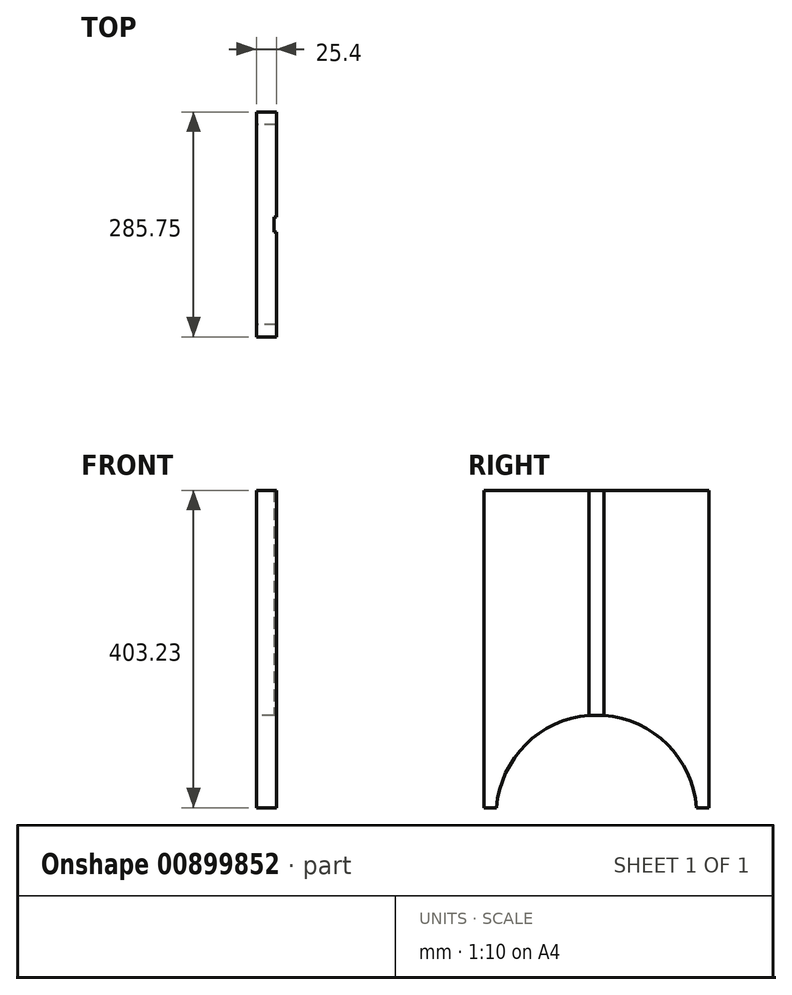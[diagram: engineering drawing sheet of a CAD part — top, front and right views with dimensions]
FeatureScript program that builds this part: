
annotation { "Feature Type Name" : "Feature", "Feature Type Description" : "" }
export const myFeature = defineFeature(function(context is Context, id is Id, definition is map)
    precondition{}
    {
        {
            var Q0;
            Q0=qCreatedBy(makeId("Right.planeOp"),FACE);
            var sketch = newSketch(context, id + "F0", { "sketchPlane" : qUnion([Q0])});
            skLineSegment(sketch, "E0", {"start": v(-357.11, 338.59) * mm, "end": v(-71.36, 338.59) * mm});
            skLineSegment(sketch, "E1", {"start": v(-71.36, 338.59) * mm, "end": v(-71.36, -64.64) * mm});
            skLineSegment(sketch, "E2", {"start": v(-71.36, -64.64) * mm, "end": v(-87.24, -64.64) * mm});
            skArc(sketch, "E3", {"start": v(-87.24, -64.64) * mm, "mid": v(-214.24, 52.84) * mm, "end": v(-341.24, -64.64) * mm});
            skLineSegment(sketch, "E4", {"start": v(-357.11, 338.59) * mm, "end": v(-357.11, -64.64) * mm});
            skLineSegment(sketch, "E5", {"start": v(-357.11, -64.64) * mm, "end": v(-341.24, -64.64) * mm});
            skSolve(sketch);
        }
        {
            var Q0;
            Q0 = qSketchRegion(id + "F0", true);
            extrude(context, id + "F1", {"entities" : qUnion([Q0]), "depth" : 25.4 * mm, "offsetDistance" : 25.4 * mm});
        }
        {
            var Q0;
            Q0=makeQuery(id+"F1.opExtrude","CAP_FACE",FACE,{"disambiguationData":[OSD([sQuery(id+"F0.wireOp",EDGE,"E0"),sQuery(id+"F0.wireOp",EDGE,"E1"),sQuery(id+"F0.wireOp",EDGE,"E2"),sQuery(id+"F0.wireOp",EDGE,"E3"),sQuery(id+"F0.wireOp",EDGE,"E4"),sQuery(id+"F0.wireOp",EDGE,"E5")])],"isStart":false});
            var sketch = newSketch(context, id + "F2", { "sketchPlane" : qUnion([Q0])});
            skLineSegment(sketch, "E6", {"start": v(-214.24, 338.59) * mm, "end": v(-223.76, 338.59) * mm});
            skLineSegment(sketch, "E7", {"start": v(-223.76, 338.59) * mm, "end": v(-223.76, 26.9) * mm});
            skLineSegment(sketch, "E8", {"start": v(-223.76, 26.9) * mm, "end": v(-204.71, 26.9) * mm});
            skLineSegment(sketch, "E9", {"start": v(-204.71, 26.9) * mm, "end": v(-204.71, 338.59) * mm});
            skLineSegment(sketch, "E10", {"start": v(-204.71, 338.59) * mm, "end": v(-214.24, 338.59) * mm});
            skSolve(sketch);
        }
        {
            var Q0;
            {var subQ2=sQuery(id+"F2.wireOp",EDGE,"E6");Q0=makeQuery(id+"F2.imprint","IMPRINT",FACE,{"disambiguationData":[TD([[makeQuery(id+"F2.imprint","IMPRINT",EDGE,{"derivedFrom":subQ2}),-1.0]])]});}
            var Q1;
            {var subQ0=sQuery(id+"F2.wireOp",EDGE,"E8");Q1=makeQuery(id+"F2.imprint","IMPRINT",FACE,{"disambiguationData":[TD([[makeQuery(id+"F2.imprint","IMPRINT",EDGE,{"derivedFrom":subQ0}),1.0]])]});}
            extrude(context, id + "F3", {"entities" : qUnion([Q0, Q1]), "operationType" : NewBodyOperationType.REMOVE, "oppositeDirection" : true, "depth" : 3.17 * mm, "offsetDistance" : 25.4 * mm});
        }
    });
